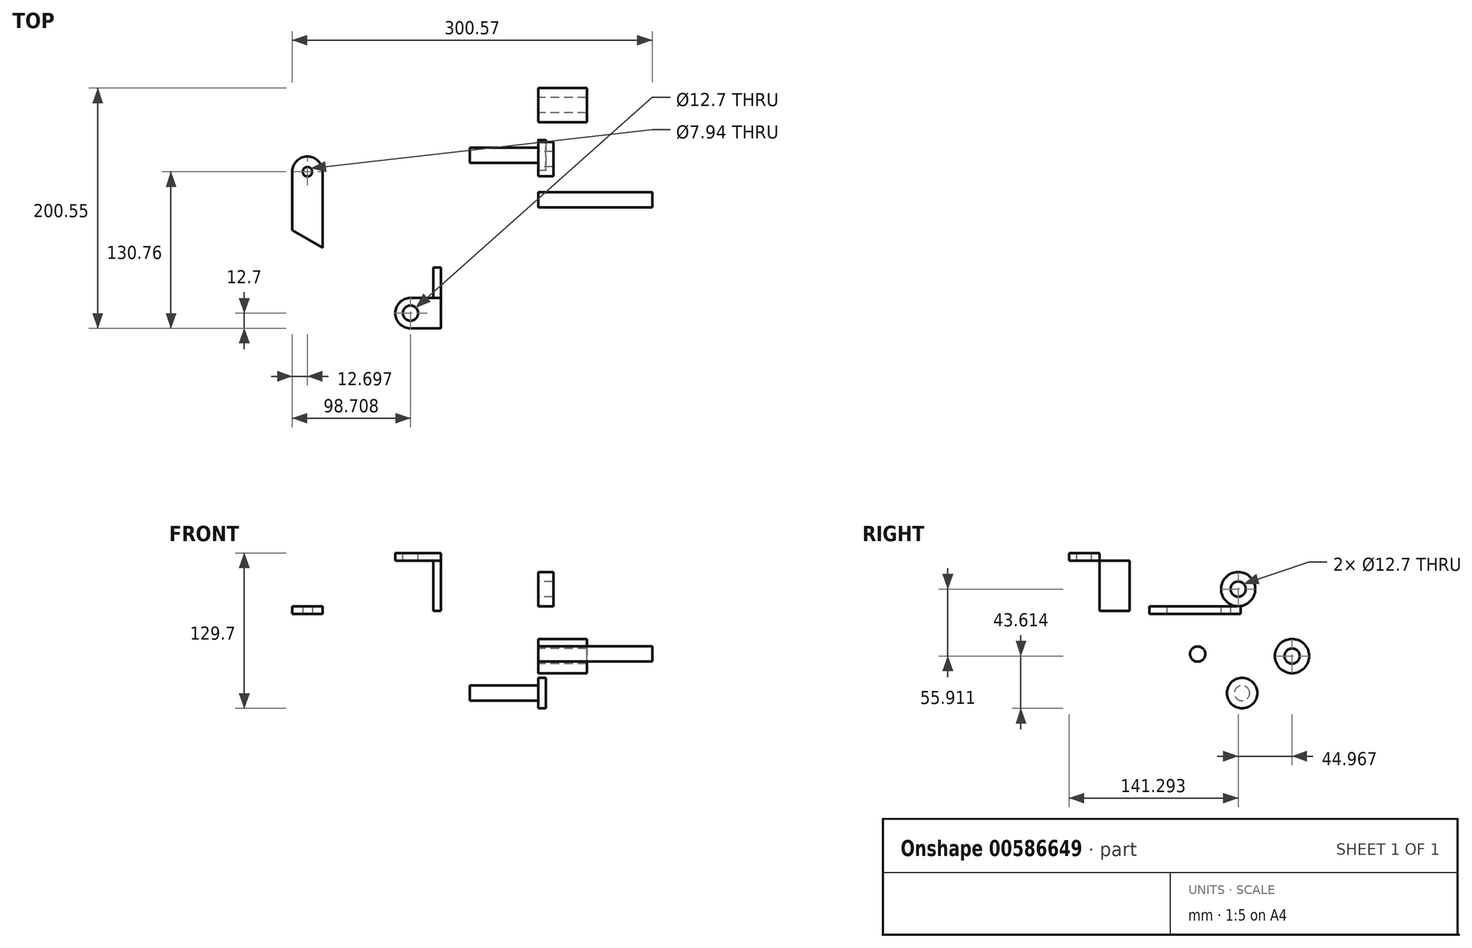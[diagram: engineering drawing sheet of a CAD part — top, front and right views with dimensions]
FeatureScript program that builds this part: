
annotation { "Feature Type Name" : "Feature", "Feature Type Description" : "" }
export const myFeature = defineFeature(function(context is Context, id is Id, definition is map)
    precondition{}
    {
        {
            var Q0;
            Q0=qCreatedBy(makeId("Front.planeOp"),FACE);
            var sketch = newSketch(context, id + "F0", { "sketchPlane" : qUnion([Q0])});
            skLineSegment(sketch, "E0.bottom", {"start": v(-87.56, 44.43) * mm, "end": v(-81.21, 44.43) * mm});
            skLineSegment(sketch, "E0.top", {"start": v(-87.56, 2.52) * mm, "end": v(-81.21, 2.52) * mm});
            skLineSegment(sketch, "E0.left", {"start": v(-87.56, 44.43) * mm, "end": v(-87.56, 2.52) * mm});
            skLineSegment(sketch, "E0.right", {"start": v(-81.21, 44.43) * mm, "end": v(-81.21, 2.52) * mm});
            skSolve(sketch);
        }
        {
            var Q0;
            Q0=makeQuery(id+"F0.imprint","IMPRINT",FACE,{"disambiguationData":[TD([[makeQuery(id+"F0.imprint","IMPRINT",EDGE,{"derivedFrom":sQuery(id+"F0.wireOp",EDGE,"E0.bottom")}),-1.0]])]});
            extrude(context, id + "F1", {"entities" : qUnion([Q0]), "depth" : 25.4 * mm, "offsetDistance" : 25.4 * mm});
        }
        {
            var Q0;
            Q0=makeQuery(id+"F1.opExtrude","CAP_FACE",FACE,{"disambiguationData":[OSD([sQuery(id+"F0.wireOp",EDGE,"E0.bottom"),sQuery(id+"F0.wireOp",EDGE,"E0.top"),sQuery(id+"F0.wireOp",EDGE,"E0.left"),sQuery(id+"F0.wireOp",EDGE,"E0.right")])],"isStart":false});
            var sketch = newSketch(context, id + "F2", { "sketchPlane" : qUnion([Q0])});
            skLineSegment(sketch, "E1.bottom", {"start": v(-81.21, 44.43) * mm, "end": v(-119.31, 44.43) * mm});
            skLineSegment(sketch, "E1.top", {"start": v(-81.21, 50.78) * mm, "end": v(-119.31, 50.78) * mm});
            skLineSegment(sketch, "E1.left", {"start": v(-81.21, 44.43) * mm, "end": v(-81.21, 50.78) * mm});
            skLineSegment(sketch, "E1.right", {"start": v(-119.31, 44.43) * mm, "end": v(-119.31, 50.78) * mm});
            skSolve(sketch);
        }
        {
            var Q0;
            Q0=makeQuery(id+"F2.imprint","IMPRINT",FACE,{"disambiguationData":[TD([[makeQuery(id+"F2.imprint","IMPRINT",EDGE,{"derivedFrom":sQuery(id+"F2.wireOp",EDGE,"E1.top")}),1.0]])]});
            extrude(context, id + "F3", {"entities" : qUnion([Q0]), "depth" : 25.4 * mm, "offsetDistance" : 25.4 * mm});
        }
        {
            var Q0;
            Q0=makeQuery(id+"F3.opExtrude","SWEPT_FACE",FACE,{"disambiguationData":[OSD([sQuery(id+"F2.wireOp",EDGE,"E1.top")])]});
            var sketch = newSketch(context, id + "F4", { "sketchPlane" : qUnion([Q0])});
            skCircle(sketch, "E2", {"center": v(-106.61, -38.1) * mm, "radius": 6.35 * mm});
            skSolve(sketch);
        }
        {
            var Q0;
            Q0=makeQuery(id+"F4.imprint","IMPRINT",FACE,{"disambiguationData":[TD([[makeQuery(id+"F4.imprint","IMPRINT",EDGE,{"derivedFrom":sQuery(id+"F4.wireOp",EDGE,"E2")}),1.0]])]});
            var Q1;
            Q1=makeQuery(id+"F3.opExtrude","SWEPT_FACE",FACE,{"disambiguationData":[OSD([sQuery(id+"F2.wireOp",EDGE,"E1.bottom")])]});
            extrude(context, id + "F5", {"entities" : qUnion([Q0]), "operationType" : NewBodyOperationType.REMOVE, "endBound" : BoundingType.UP_TO_SURFACE, "oppositeDirection" : true, "depth" : 25.4 * mm, "endBoundEntityFace" : qUnion([Q1]), "offsetDistance" : 25.4 * mm});
        }
        {
            var Q0;
            Q0=qCreatedBy(makeId("Right.planeOp"),FACE);
            var sketch = newSketch(context, id + "F6", { "sketchPlane" : qUnion([Q0])});
            skCircle(sketch, "E3", {"center": v(90.5, 20.6) * mm, "radius": 14.29 * mm});
            skCircle(sketch, "E4", {"center": v(90.5, 20.6) * mm, "radius": 6.35 * mm});
            skSolve(sketch);
        }
        {
            var Q0;
            Q0=makeQuery(id+"F6.imprint","IMPRINT",FACE,{"disambiguationData":[TD([[makeQuery(id+"F6.imprint","IMPRINT",EDGE,{"derivedFrom":sQuery(id+"F6.wireOp",EDGE,"E3")}),1.0]])]});
            extrude(context, id + "F7", {"entities" : qUnion([Q0]), "depth" : 12.7 * mm, "offsetDistance" : 25.4 * mm});
        }
        {
            var Q0;
            Q0=qCreatedBy(makeId("Right.planeOp"),FACE);
            var sketch = newSketch(context, id + "F8", { "sketchPlane" : qUnion([Q0])});
            skCircle(sketch, "E5", {"center": v(56.66, -33.62) * mm, "radius": 6.35 * mm});
            skSolve(sketch);
        }
        {
            var Q0;
            Q0=makeQuery(id+"F8.imprint","IMPRINT",FACE,{"disambiguationData":[TD([[makeQuery(id+"F8.imprint","IMPRINT",EDGE,{"derivedFrom":sQuery(id+"F8.wireOp",EDGE,"E5")}),1.0]])]});
            extrude(context, id + "F9", {"entities" : qUnion([Q0]), "depth" : 95.25 * mm, "offsetDistance" : 25.4 * mm});
        }
        {
            var Q0;
            Q0=qCreatedBy(makeId("Right.planeOp"),FACE);
            var sketch = newSketch(context, id + "F10", { "sketchPlane" : qUnion([Q0])});
            skCircle(sketch, "E6", {"center": v(135.46, -35.3) * mm, "radius": 14.29 * mm});
            skCircle(sketch, "E7", {"center": v(135.46, -35.3) * mm, "radius": 6.35 * mm});
            skSolve(sketch);
        }
        {
            var Q0;
            Q0=makeQuery(id+"F10.imprint","IMPRINT",FACE,{"disambiguationData":[TD([[makeQuery(id+"F10.imprint","IMPRINT",EDGE,{"derivedFrom":sQuery(id+"F10.wireOp",EDGE,"E6")}),1.0]])]});
            extrude(context, id + "F11", {"entities" : qUnion([Q0]), "depth" : 40.64 * mm, "offsetDistance" : 25.4 * mm});
        }
        {
            var Q0;
            Q0=qCreatedBy(makeId("Right.planeOp"),FACE);
            var sketch = newSketch(context, id + "F12", { "sketchPlane" : qUnion([Q0])});
            skCircle(sketch, "E8", {"center": v(93.73, -66.22) * mm, "radius": 12.7 * mm});
            skSolve(sketch);
        }
        {
            var Q0;
            Q0=makeQuery(id+"F12.imprint","IMPRINT",FACE,{"disambiguationData":[TD([[makeQuery(id+"F12.imprint","IMPRINT",EDGE,{"derivedFrom":sQuery(id+"F12.wireOp",EDGE,"E8")}),1.0]])]});
            extrude(context, id + "F13", {"entities" : qUnion([Q0]), "depth" : 6.35 * mm, "offsetDistance" : 25.4 * mm});
        }
        {
            var Q0;
            Q0=makeQuery(id+"F13.opExtrude","CAP_FACE",FACE,{"disambiguationData":[OSD([sQuery(id+"F12.wireOp",EDGE,"E8")])],"isStart":true});
            var sketch = newSketch(context, id + "F14", { "sketchPlane" : qUnion([Q0])});
            skCircle(sketch, "E9", {"center": v(-93.73, -66.22) * mm, "radius": 6.35 * mm});
            skSolve(sketch);
        }
        {
            var Q0;
            Q0=makeQuery(id+"F14.imprint","IMPRINT",FACE,{"disambiguationData":[TD([[makeQuery(id+"F14.imprint","IMPRINT",EDGE,{"derivedFrom":sQuery(id+"F14.wireOp",EDGE,"E9")}),1.0]])]});
            extrude(context, id + "F15", {"entities" : qUnion([Q0]), "operationType" : NewBodyOperationType.ADD, "depth" : 57.15 * mm, "offsetDistance" : 25.4 * mm});
        }
        {
            var Q0;
            Q0=qCreatedBy(makeId("Top.planeOp"),FACE);
            var sketch = newSketch(context, id + "F16", { "sketchPlane" : qUnion([Q0])});
            skLineSegment(sketch, "E10", {"start": v(-192.62, 92.66) * mm, "end": v(-192.62, 92.66) * mm});
            skLineSegment(sketch, "E11", {"start": v(-179.92, 79.96) * mm, "end": v(-179.92, 16.46) * mm});
            skLineSegment(sketch, "E12", {"start": v(-179.92, 16.46) * mm, "end": v(-205.32, 31.12) * mm});
            skLineSegment(sketch, "E13", {"start": v(-205.32, 31.12) * mm, "end": v(-205.32, 79.96) * mm});
            skCircle(sketch, "E14", {"center": v(-192.62, 79.96) * mm, "radius": 3.97 * mm});
            skPoint(sketch, "E15.visualSharp", {"position": v(-205.32, 92.66) * mm});
            skArc(sketch, "E15.filletArc", {"start": v(-192.62, 92.66) * mm, "mid": v(-201.6, 88.94) * mm, "end": v(-205.32, 79.96) * mm});
            skPoint(sketch, "E16.visualSharp", {"position": v(-179.92, 92.66) * mm});
            skArc(sketch, "E16.filletArc", {"start": v(-179.92, 79.96) * mm, "mid": v(-183.64, 88.94) * mm, "end": v(-192.62, 92.66) * mm});
            skSolve(sketch);
        }
        {
            var Q0;
            Q0=makeQuery(id+"F16.imprint","IMPRINT",FACE,{"disambiguationData":[TD([[makeQuery(id+"F16.imprint","IMPRINT",EDGE,{"derivedFrom":sQuery(id+"F16.wireOp",EDGE,"E11")}),-1.0]])]});
            extrude(context, id + "F17", {"entities" : qUnion([Q0]), "depth" : 6.35 * mm, "offsetDistance" : 25.4 * mm});
        }
        {
            var Q0;
            Q0=makeQuery(id+"F3.opExtrude","CAP_EDGE",EDGE,{"disambiguationData":[OSD([sQuery(id+"F2.wireOp",EDGE,"E1.right")])],"isStart":false});
            var Q1;
            Q1=makeQuery(id+"F3.opExtrude","CAP_EDGE",EDGE,{"disambiguationData":[OSD([sQuery(id+"F2.wireOp",EDGE,"E1.right")])],"isStart":true});
            fillet(context, id + "F18", {"entities" : qUnion([Q0, Q1]), "radius" : 12.7 * mm, "tangentPropagation" : true, "allowEdgeOverflow" : false});
        }
    });
